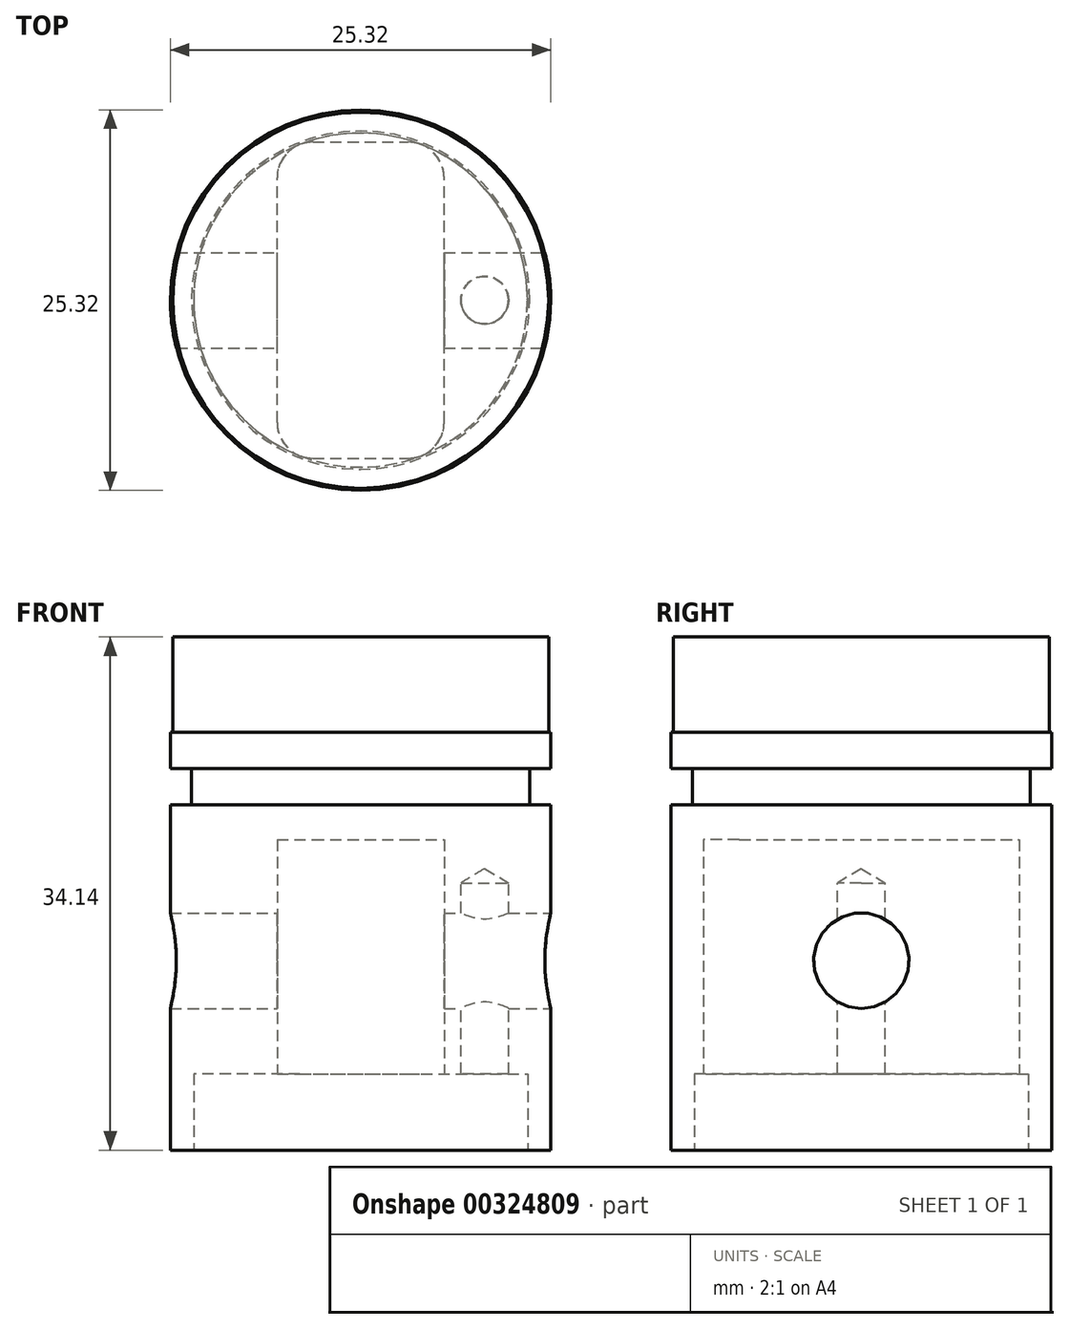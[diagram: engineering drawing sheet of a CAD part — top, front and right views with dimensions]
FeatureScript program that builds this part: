
annotation { "Feature Type Name" : "Feature", "Feature Type Description" : "" }
export const myFeature = defineFeature(function(context is Context, id is Id, definition is map)
    precondition{}
    {
        {
            var Q0;
            Q0=qCreatedBy(makeId("Top.planeOp"),FACE);
            var sketch = newSketch(context, id + "F0", { "sketchPlane" : qUnion([Q0])});
            skCircle(sketch, "E0", {"center": v(0, 0) * mm, "radius": 12.66 * mm});
            skSolve(sketch);
        }
        {
            var Q0;
            Q0=makeQuery(id+"F0.imprint","IMPRINT",FACE,{"disambiguationData":[TD([[makeQuery(id+"F0.imprint","IMPRINT",EDGE,{"derivedFrom":sQuery(id+"F0.wireOp",EDGE,"E0")}),1.0]])]});
            extrude(context, id + "F1", {"entities" : qUnion([Q0]), "depth" : 34.14 * mm, "offsetDistance" : 25.4 * mm});
        }
        {
            var Q0;
            Q0=makeQuery(id+"F1.opExtrude","CAP_FACE",FACE,{"disambiguationData":[OSD([sQuery(id+"F0.wireOp",EDGE,"E0")])],"isStart":false});
            var sketch = newSketch(context, id + "F2", { "sketchPlane" : qUnion([Q0])});
            skCircle(sketch, "E1", {"center": v(0, 0) * mm, "radius": 12.5 * mm});
            skSolve(sketch);
        }
        {
            var Q0;
            Q0=makeQuery(id+"F2.imprint","IMPRINT",FACE,{"disambiguationData":[TD([[makeQuery(id+"F2.imprint","IMPRINT",EDGE,{"derivedFrom":sQuery(id+"F2.wireOp",EDGE,"E1")}),-1.0]])]});
            extrude(context, id + "F3", {"entities" : qUnion([Q0]), "operationType" : NewBodyOperationType.REMOVE, "oppositeDirection" : true, "depth" : 6.35 * mm, "offsetDistance" : 25.4 * mm});
        }
        {
            var Q0;
            Q0=qCreatedBy(makeId("Front.planeOp"),FACE);
            var sketch = newSketch(context, id + "F4", { "sketchPlane" : qUnion([Q0])});
            skLineSegment(sketch, "E2.bottom", {"start": v(11.25, 25.37) * mm, "end": v(14.01, 25.37) * mm});
            skLineSegment(sketch, "E2.top", {"start": v(11.25, 22.99) * mm, "end": v(14.01, 22.99) * mm});
            skLineSegment(sketch, "E2.left", {"start": v(11.25, 25.37) * mm, "end": v(11.25, 22.99) * mm});
            skLineSegment(sketch, "E2.right", {"start": v(14.01, 25.37) * mm, "end": v(14.01, 22.99) * mm});
            skSolve(sketch);
        }
        {
            var Q0;
            Q0=makeQuery(id+"F4.imprint","IMPRINT",FACE,{"disambiguationData":[TD([[makeQuery(id+"F4.imprint","IMPRINT",EDGE,{"derivedFrom":sQuery(id+"F4.wireOp",EDGE,"E2.bottom")}),-1.0]])]});
            var Q1;
            Q1=makeQuery(id+"F1.opExtrude","CAP_EDGE",EDGE,{"disambiguationData":[OSD([sQuery(id+"F0.wireOp",EDGE,"E0")])],"isStart":true});
            sweep(context, id + "F5", {"operationType" : NewBodyOperationType.REMOVE, "profiles" : qUnion([Q0]), "path" : qUnion([Q1])});
        }
        {
            var Q0;
            Q0=qCreatedBy(makeId("Right.planeOp"),FACE);
            cPlane(context, id + "F6", {"entities" : qUnion([Q0]), "cplaneType" : CPlaneType.OFFSET, "offset" : 12.7 * mm, "width" : 152.4 * mm, "height" : 152.4 * mm});
        }
        {
            var Q0;
            Q0=qCreatedBy(id+"F6.planeOp",FACE);
            var sketch = newSketch(context, id + "F7", { "sketchPlane" : qUnion([Q0])});
            skCircle(sketch, "E3", {"center": v(0, 12.6) * mm, "radius": 3.18 * mm});
            skSolve(sketch);
        }
        {
            var Q0;
            Q0=makeQuery(id+"F7.imprint","IMPRINT",FACE,{"disambiguationData":[TD([[makeQuery(id+"F7.imprint","IMPRINT",EDGE,{"derivedFrom":sQuery(id+"F7.wireOp",EDGE,"E3")}),1.0]])]});
            extrude(context, id + "F8", {"entities" : qUnion([Q0]), "operationType" : NewBodyOperationType.REMOVE, "endBound" : BoundingType.THROUGH_ALL, "oppositeDirection" : true, "depth" : 25.4 * mm, "offsetDistance" : 25.4 * mm});
        }
        {
            var Q0;
            Q0=makeQuery(id+"F1.opExtrude","CAP_FACE",FACE,{"disambiguationData":[OSD([sQuery(id+"F0.wireOp",EDGE,"E0")])],"isStart":true});
            var sketch = newSketch(context, id + "F9", { "sketchPlane" : qUnion([Q0])});
            skCircle(sketch, "E4", {"center": v(0, 0) * mm, "radius": 11.11 * mm});
            skSolve(sketch);
        }
        {
            var Q0;
            Q0=makeQuery(id+"F9.imprint","IMPRINT",FACE,{"disambiguationData":[TD([[makeQuery(id+"F9.imprint","IMPRINT",EDGE,{"derivedFrom":sQuery(id+"F9.wireOp",EDGE,"E4")}),1.0]])]});
            extrude(context, id + "F10", {"entities" : qUnion([Q0]), "operationType" : NewBodyOperationType.REMOVE, "oppositeDirection" : true, "depth" : 5.08 * mm, "offsetDistance" : 25.4 * mm});
        }
        {
            var Q0;
            {var subQ0=sQuery(id+"F9.wireOp",EDGE,"E4");var subQ1=makeQuery(id+"F10.boolean.opBoolean","COPY",FACE,{"derivedFrom":makeQuery(id+"F10.opExtrude","CAP_FACE",FACE,{"disambiguationData":[OSD([subQ0])],"isStart":false})});Q0=makeQuery(id+"F06nXd2fXCxFe3R_1.boolean.opBoolean","SPLIT",FACE,{"disambiguationData":[TD([makeQuery(id+"F06nXd2fXCxFe3R_1.opExtrude","SWEPT_FACE",FACE,{"disambiguationData":[OSD([sQuery(id+"FnOW64V1skJAZom_1.wireOp",EDGE,"j77vrDcH-ontL-8Oww-tWwY-meUzddnfOAOM.right")])]})])],"derivedFrom":subQ1});}
            var sketch = newSketch(context, id + "F11", { "sketchPlane" : qUnion([Q0])});
            skPoint(sketch, "E5", {"position": v(8.26, 0) * mm});
            skSolve(sketch);
        }
        {
            var Q0;
            Q0=sQuery(id+"F11.wireOp",VERTEX,"E5");
            var Q1;
            Q1=makeQuery(id+"F1.opExtrude","SWEPT_BODY",BODY,{"disambiguationData":[OSD([sQuery(id+"F0.wireOp",EDGE,"E0")])]});
            hole(context, id + "F12", {"style" : HoleStyle.SIMPLE, "endStyle" : HoleEndStyle.BLIND, "holeDiameter" : 3.17 * mm, "majorDiameter" : 6.35 * mm, "holeDepth" : 12.7 * mm, "tappedDepth" : 12.7 * mm, "tapClearance" : 3, "locations" : qUnion([Q0]), "scope" : qUnion([Q1])});
        }
        {
            var Q0;
            Q0=makeQuery(id+"F1.opExtrude","CAP_FACE",FACE,{"disambiguationData":[OSD([sQuery(id+"F0.wireOp",EDGE,"E0")])],"isStart":true});
            var sketch = newSketch(context, id + "F13", { "sketchPlane" : qUnion([Q0])});
            skLineSegment(sketch, "E6", {"start": v(0, 0) * mm, "end": v(-7.17, 18.38) * mm, "construction": true});
            skArc(sketch, "E7", {"start": v(-3.17, 10.52) * mm, "mid": v(-4.86, 9.82) * mm, "end": v(-5.56, 8.13) * mm});
            skArc(sketch, "E8.MirrorC", {"start": v(3.17, 10.52) * mm, "mid": v(4.86, 9.82) * mm, "end": v(5.56, 8.13) * mm});
            skLineSegment(sketch, "E9", {"start": v(-3.17, 10.52) * mm, "end": v(3.17, 10.52) * mm});
            skLineSegment(sketch, "E10.MirrorCS", {"start": v(-3.17, -10.52) * mm, "end": v(3.17, -10.52) * mm});
            skArc(sketch, "E11.MirrorC", {"start": v(-3.17, -10.52) * mm, "mid": v(-4.86, -9.82) * mm, "end": v(-5.56, -8.13) * mm});
            skArc(sketch, "E12.MirrorC", {"start": v(3.17, -10.52) * mm, "mid": v(4.86, -9.82) * mm, "end": v(5.56, -8.13) * mm});
            skLineSegment(sketch, "E13", {"start": v(-5.56, 8.13) * mm, "end": v(-5.56, -8.13) * mm});
            skLineSegment(sketch, "E14.MirrorCS", {"start": v(5.56, 8.13) * mm, "end": v(5.56, -8.13) * mm});
            skSolve(sketch);
        }
        {
            var Q0;
            {var subQ8=sQuery(id+"F13.wireOp",EDGE,"E9");Q0=makeQuery(id+"F13.imprint","IMPRINT",FACE,{"disambiguationData":[TD([[makeQuery(id+"F13.imprint","IMPRINT",EDGE,{"derivedFrom":subQ8}),-1.0]])]});}
            extrude(context, id + "F14", {"entities" : qUnion([Q0]), "operationType" : NewBodyOperationType.REMOVE, "oppositeDirection" : true, "depth" : 20.65 * mm, "offsetDistance" : 25.4 * mm});
        }
    });
